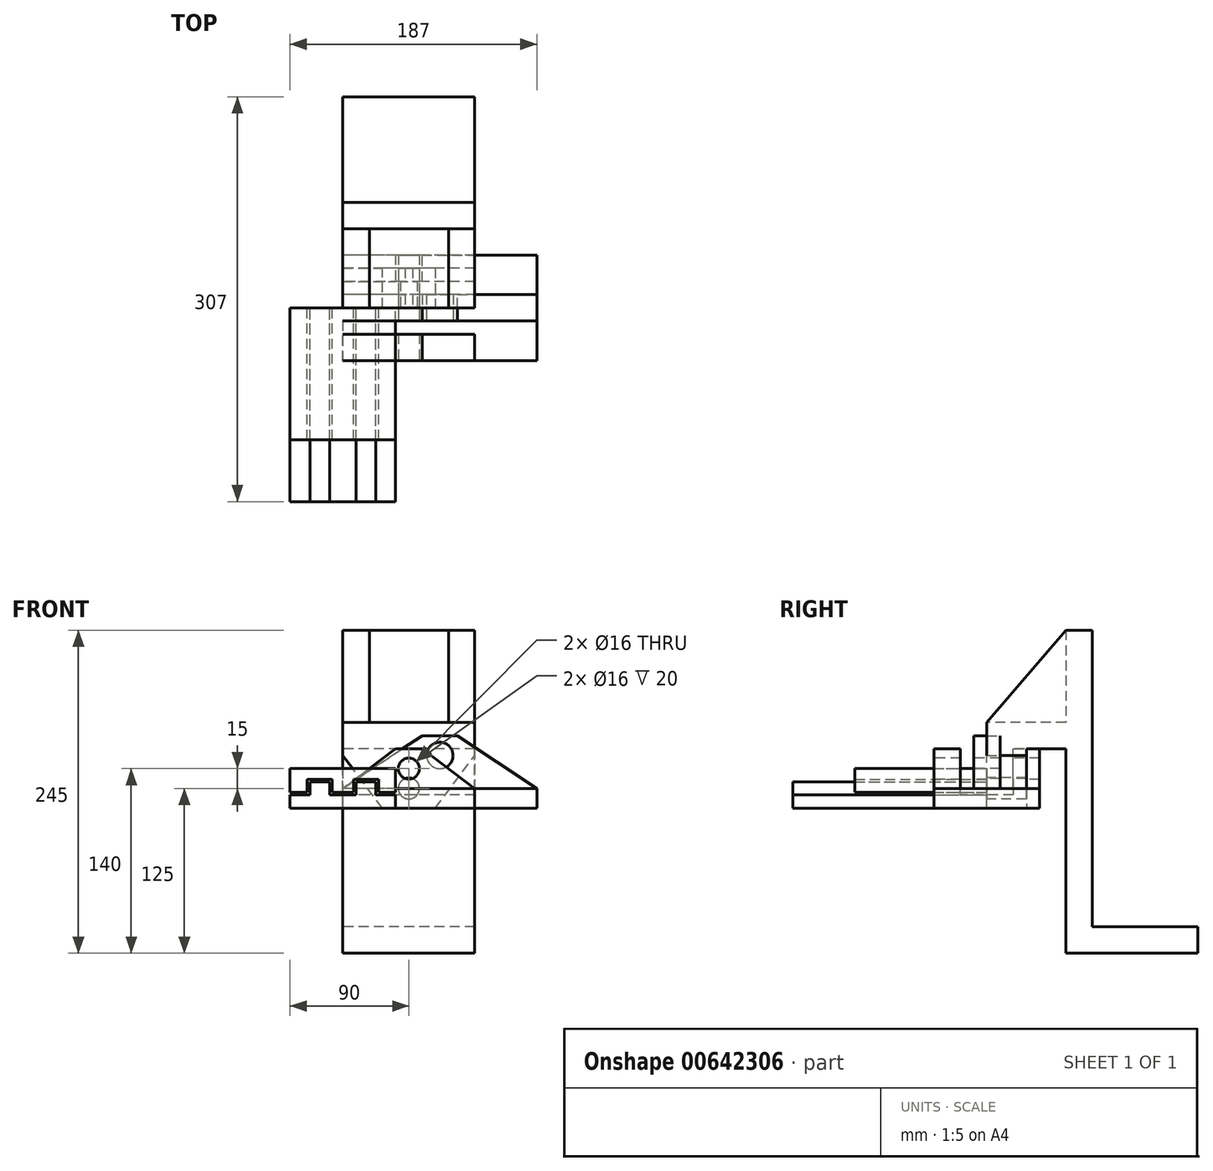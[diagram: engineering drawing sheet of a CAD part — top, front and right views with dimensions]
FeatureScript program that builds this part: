
annotation { "Feature Type Name" : "Feature", "Feature Type Description" : "" }
export const myFeature = defineFeature(function(context is Context, id is Id, definition is map)
    precondition{}
    {
        {
            var Q0;
            Q0=qCreatedBy(makeId("Right.planeOp"),FACE);
            var sketch = newSketch(context, id + "F0", { "sketchPlane" : qUnion([Q0])});
            skLineSegment(sketch, "E0", {"start": v(0, 0) * mm, "end": v(40, 0) * mm});
            skLineSegment(sketch, "E1", {"start": v(40, 0) * mm, "end": v(40, 15) * mm});
            skLineSegment(sketch, "E2", {"start": v(40, 15) * mm, "end": v(10, 15) * mm});
            skLineSegment(sketch, "E3", {"start": v(10, 15) * mm, "end": v(10, 55) * mm});
            skLineSegment(sketch, "E4", {"start": v(10, 55) * mm, "end": v(-10, 55) * mm});
            skLineSegment(sketch, "E5", {"start": v(-10, 55) * mm, "end": v(-10, 15) * mm});
            skLineSegment(sketch, "E6", {"start": v(-10, 15) * mm, "end": v(-40, 15) * mm});
            skLineSegment(sketch, "E7", {"start": v(-40, 15) * mm, "end": v(-40, 0) * mm});
            skLineSegment(sketch, "E8", {"start": v(-40, 0) * mm, "end": v(0, 0) * mm});
            skSolve(sketch);
        }
        {
            var Q0;
            Q0=makeQuery(id+"F0.imprint","IMPRINT",FACE,{"disambiguationData":[TD([[makeQuery(id+"F0.imprint","IMPRINT",EDGE,{"derivedFrom":sQuery(id+"F0.wireOp",EDGE,"E0")}),1.0]])]});
            extrude(context, id + "F1", {"entities" : qUnion([Q0]), "depth" : 147 * mm, "offsetDistance" : 25 * mm});
        }
        {
            var Q0;
            Q0=makeQuery(id+"F1.opExtrude","CAP_EDGE",EDGE,{"disambiguationData":[OSD([sQuery(id+"F0.wireOp",EDGE,"E4")])],"isStart":false});
            var Q1;
            Q1=makeQuery(id+"F1.opExtrude","CAP_EDGE",EDGE,{"disambiguationData":[OSD([sQuery(id+"F0.wireOp",EDGE,"E4")])],"isStart":true});
            chamfer(context, id + "F2", {"entities" : qUnion([Q0, Q1]), "chamferType" : ChamferType.TWO_OFFSETS, "width1" : 40 * mm, "oppositeDirection" : false, "width2" : 60 * mm, "tangentPropagation" : true});
        }
        {
            var Q0;
            Q0=makeQuery(id+"F1.opExtrude","SWEPT_FACE",FACE,{"disambiguationData":[OSD([sQuery(id+"F0.wireOp",EDGE,"E5")])]});
            var sketch = newSketch(context, id + "F3", { "sketchPlane" : qUnion([Q0])});
            skCircle(sketch, "E9", {"center": v(73.5, 40) * mm, "radius": 10 * mm});
            skPoint(sketch, "E9.centerSnap0", {"position": v(73.5, 55) * mm});
            skSolve(sketch);
        }
        {
            var Q0;
            Q0=makeQuery(id+"F3.imprint","IMPRINT",FACE,{"disambiguationData":[TD([[makeQuery(id+"F3.imprint","IMPRINT",EDGE,{"derivedFrom":sQuery(id+"F3.wireOp",EDGE,"E9")}),1.0]])]});
            extrude(context, id + "F4", {"entities" : qUnion([Q0]), "operationType" : NewBodyOperationType.REMOVE, "endBound" : BoundingType.THROUGH_ALL, "oppositeDirection" : true, "depth" : 25 * mm, "offsetDistance" : 25 * mm});
        }
        {
            var Q0;
            Q0=qCreatedBy(makeId("Front.planeOp"),FACE);
            var sketch = newSketch(context, id + "F5", { "sketchPlane" : qUnion([Q0])});
            skLineSegment(sketch, "E10", {"start": v(0, 0) * mm, "end": v(40, 0) * mm});
            skLineSegment(sketch, "E11", {"start": v(40, 0) * mm, "end": v(40, 10) * mm});
            skLineSegment(sketch, "E12", {"start": v(40, 10) * mm, "end": v(25, 10) * mm});
            skLineSegment(sketch, "E13", {"start": v(25, 10) * mm, "end": v(25, 20) * mm});
            skLineSegment(sketch, "E14", {"start": v(25, 20) * mm, "end": v(10, 20) * mm});
            skLineSegment(sketch, "E15", {"start": v(10, 20) * mm, "end": v(10, 10) * mm});
            skLineSegment(sketch, "E16", {"start": v(10, 10) * mm, "end": v(-10, 10) * mm});
            skLineSegment(sketch, "E17", {"start": v(-10, 10) * mm, "end": v(-10, 20) * mm});
            skLineSegment(sketch, "E18", {"start": v(-10, 20) * mm, "end": v(-25, 20) * mm});
            skLineSegment(sketch, "E19", {"start": v(-25, 20) * mm, "end": v(-25, 10) * mm});
            skLineSegment(sketch, "E20", {"start": v(-25, 10) * mm, "end": v(-40, 10) * mm});
            skLineSegment(sketch, "E21", {"start": v(-40, 10) * mm, "end": v(-40, 0) * mm});
            skLineSegment(sketch, "E22", {"start": v(-40, 0) * mm, "end": v(0, 0) * mm});
            skLineSegment(sketch, "E23", {"start": v(-40, 12) * mm, "end": v(-27, 12) * mm});
            skLineSegment(sketch, "E24", {"start": v(-27, 12) * mm, "end": v(-27, 22) * mm});
            skLineSegment(sketch, "E25", {"start": v(-27, 22) * mm, "end": v(-8, 22) * mm});
            skLineSegment(sketch, "E26", {"start": v(-8, 22) * mm, "end": v(-8, 12) * mm});
            skLineSegment(sketch, "E27", {"start": v(-8, 12) * mm, "end": v(8, 12) * mm});
            skLineSegment(sketch, "E28", {"start": v(8, 12) * mm, "end": v(8, 22) * mm});
            skLineSegment(sketch, "E29", {"start": v(8, 22) * mm, "end": v(27, 22) * mm});
            skLineSegment(sketch, "E30", {"start": v(27, 22) * mm, "end": v(27, 12) * mm});
            skLineSegment(sketch, "E31", {"start": v(27, 12) * mm, "end": v(40, 12) * mm});
            skLineSegment(sketch, "E32", {"start": v(40, 12) * mm, "end": v(40, 30) * mm});
            skLineSegment(sketch, "E33", {"start": v(40, 30) * mm, "end": v(-40, 30) * mm});
            skLineSegment(sketch, "E34", {"start": v(-40, 30) * mm, "end": v(-40, 12) * mm});
            skSolve(sketch);
        }
        {
            var Q0;
            Q0=makeQuery(id+"F5.imprint","IMPRINT",FACE,{"disambiguationData":[TD([[makeQuery(id+"F5.imprint","IMPRINT",EDGE,{"derivedFrom":sQuery(id+"F5.wireOp",EDGE,"E10")}),1.0]])]});
            extrude(context, id + "F6", {"entities" : qUnion([Q0]), "depth" : 147 * mm, "offsetDistance" : 25 * mm});
        }
        {
            var Q0;
            Q0=makeQuery(id+"F5.imprint","IMPRINT",FACE,{"disambiguationData":[TD([[makeQuery(id+"F5.imprint","IMPRINT",EDGE,{"derivedFrom":sQuery(id+"F5.wireOp",EDGE,"E23")}),1.0]])]});
            extrude(context, id + "F7", {"entities" : qUnion([Q0]), "depth" : 100 * mm, "offsetDistance" : 25 * mm});
        }
        {
            var Q0;
            Q0=qCreatedBy(makeId("Right.planeOp"),FACE);
            var sketch = newSketch(context, id + "F8", { "sketchPlane" : qUnion([Q0])});
            skLineSegment(sketch, "E35", {"start": v(0, 0) * mm, "end": v(40, 0) * mm});
            skLineSegment(sketch, "E36", {"start": v(40, 0) * mm, "end": v(40, 45) * mm});
            skLineSegment(sketch, "E37", {"start": v(40, 45) * mm, "end": v(20, 45) * mm});
            skLineSegment(sketch, "E38", {"start": v(20, 45) * mm, "end": v(20, 10) * mm});
            skLineSegment(sketch, "E39", {"start": v(20, 10) * mm, "end": v(-20, 10) * mm});
            skLineSegment(sketch, "E40", {"start": v(-20, 10) * mm, "end": v(-20, 45) * mm});
            skLineSegment(sketch, "E41", {"start": v(-20, 45) * mm, "end": v(-40, 45) * mm});
            skLineSegment(sketch, "E42", {"start": v(-40, 45) * mm, "end": v(-40, 0) * mm});
            skLineSegment(sketch, "E43", {"start": v(-40, 0) * mm, "end": v(0, 0) * mm});
            skSolve(sketch);
        }
        {
            var Q0;
            Q0=makeQuery(id+"F8.imprint","IMPRINT",FACE,{"disambiguationData":[TD([[makeQuery(id+"F8.imprint","IMPRINT",EDGE,{"derivedFrom":sQuery(id+"F8.wireOp",EDGE,"E35")}),1.0]])]});
            extrude(context, id + "F9", {"entities" : qUnion([Q0]), "depth" : 100 * mm, "offsetDistance" : 25 * mm});
        }
        {
            var Q0;
            Q0=makeQuery(id+"F9.opExtrude","SWEPT_FACE",FACE,{"disambiguationData":[OSD([sQuery(id+"F8.wireOp",EDGE,"E42")])]});
            var sketch = newSketch(context, id + "F10", { "sketchPlane" : qUnion([Q0])});
            skCircle(sketch, "E44", {"center": v(50, 30) * mm, "radius": 8 * mm});
            skPoint(sketch, "E44.centerSnap0", {"position": v(100, 22.5) * mm});
            skPoint(sketch, "E44.centerSnap1", {"position": v(50, 45) * mm});
            skSolve(sketch);
        }
        {
            var Q0;
            Q0=makeQuery(id+"F10.imprint","IMPRINT",FACE,{"disambiguationData":[TD([[makeQuery(id+"F10.imprint","IMPRINT",EDGE,{"derivedFrom":sQuery(id+"F10.wireOp",EDGE,"E44")}),1.0]])]});
            extrude(context, id + "F11", {"entities" : qUnion([Q0]), "operationType" : NewBodyOperationType.REMOVE, "endBound" : BoundingType.THROUGH_ALL, "oppositeDirection" : true, "depth" : 25 * mm, "offsetDistance" : 25 * mm});
        }
        {
            var Q0;
            Q0=makeQuery(id+"F9.opExtrude","CAP_EDGE",EDGE,{"disambiguationData":[OSD([sQuery(id+"F8.wireOp",EDGE,"E41")])],"isStart":false});
            var Q1;
            Q1=makeQuery(id+"F9.opExtrude","CAP_EDGE",EDGE,{"disambiguationData":[OSD([sQuery(id+"F8.wireOp",EDGE,"E37")])],"isStart":false});
            chamfer(context, id + "F12", {"entities" : qUnion([Q0, Q1]), "chamferType" : ChamferType.TWO_OFFSETS, "width1" : 30 * mm, "oppositeDirection" : false, "width2" : 40 * mm, "tangentPropagation" : true});
        }
        {
            var Q0;
            Q0=makeQuery(id+"F9.opExtrude","CAP_EDGE",EDGE,{"disambiguationData":[OSD([sQuery(id+"F8.wireOp",EDGE,"E37")])],"isStart":true});
            var Q1;
            Q1=makeQuery(id+"F9.opExtrude","CAP_EDGE",EDGE,{"disambiguationData":[OSD([sQuery(id+"F8.wireOp",EDGE,"E41")])],"isStart":true});
            chamfer(context, id + "F13", {"entities" : qUnion([Q0, Q1]), "chamferType" : ChamferType.TWO_OFFSETS, "width1" : 40 * mm, "oppositeDirection" : false, "width2" : 30 * mm, "tangentPropagation" : true});
        }
        {
            var Q0;
            Q0=qCreatedBy(makeId("Right.planeOp"),FACE);
            var sketch = newSketch(context, id + "F14", { "sketchPlane" : qUnion([Q0])});
            skLineSegment(sketch, "E45", {"start": v(0, 0) * mm, "end": v(30, 0) * mm});
            skLineSegment(sketch, "E46", {"start": v(30, 0) * mm, "end": v(30, 45) * mm});
            skLineSegment(sketch, "E47", {"start": v(30, 45) * mm, "end": v(60, 45) * mm});
            skLineSegment(sketch, "E48", {"start": v(60, 45) * mm, "end": v(60, -110) * mm});
            skLineSegment(sketch, "E49", {"start": v(60, -110) * mm, "end": v(160, -110) * mm});
            skLineSegment(sketch, "E50", {"start": v(160, -110) * mm, "end": v(160, -90) * mm});
            skLineSegment(sketch, "E51", {"start": v(160, -90) * mm, "end": v(80, -90) * mm});
            skLineSegment(sketch, "E52", {"start": v(80, -90) * mm, "end": v(80, 135) * mm});
            skLineSegment(sketch, "E53", {"start": v(80, 135) * mm, "end": v(60, 135) * mm});
            skLineSegment(sketch, "E54", {"start": v(60, 135) * mm, "end": v(60, 65) * mm});
            skLineSegment(sketch, "E55", {"start": v(60, 65) * mm, "end": v(0, 65) * mm});
            skLineSegment(sketch, "E56", {"start": v(0, 65) * mm, "end": v(0, 0) * mm});
            skSolve(sketch);
        }
        {
            var Q0;
            Q0=makeQuery(id+"F14.imprint","IMPRINT",FACE,{"disambiguationData":[TD([[makeQuery(id+"F14.imprint","IMPRINT",EDGE,{"derivedFrom":sQuery(id+"F14.wireOp",EDGE,"E45")}),1.0]])]});
            extrude(context, id + "F15", {"entities" : qUnion([Q0]), "depth" : 100 * mm, "offsetDistance" : 25 * mm});
        }
        {
            var Q0;
            Q0=makeQuery(id+"F15.opExtrude","SWEPT_FACE",FACE,{"disambiguationData":[OSD([sQuery(id+"F14.wireOp",EDGE,"E56")])]});
            var sketch = newSketch(context, id + "F16", { "sketchPlane" : qUnion([Q0])});
            skCircle(sketch, "E57", {"center": v(50, 15) * mm, "radius": 8 * mm});
            skPoint(sketch, "E57.centerSnap0", {"position": v(50, 0) * mm});
            skSolve(sketch);
        }
        {
            var Q0;
            Q0=makeQuery(id+"F16.imprint","IMPRINT",FACE,{"disambiguationData":[TD([[makeQuery(id+"F16.imprint","IMPRINT",EDGE,{"derivedFrom":sQuery(id+"F16.wireOp",EDGE,"E57")}),1.0]])]});
            var Q1;
            Q1=makeQuery(id+"F15.opExtrude","SWEPT_FACE",FACE,{"disambiguationData":[OSD([sQuery(id+"F14.wireOp",EDGE,"E46")])]});
            extrude(context, id + "F17", {"entities" : qUnion([Q0]), "operationType" : NewBodyOperationType.REMOVE, "endBound" : BoundingType.UP_TO_SURFACE, "oppositeDirection" : true, "depth" : 25 * mm, "endBoundEntityFace" : qUnion([Q1]), "offsetDistance" : 25 * mm});
        }
        {
            var Q0;
            Q0=makeQuery(id+"F15.opExtrude","CAP_EDGE",EDGE,{"disambiguationData":[OSD([sQuery(id+"F14.wireOp",EDGE,"E45")])],"isStart":false});
            chamfer(context, id + "F18", {"entities" : qUnion([Q0]), "chamferType" : ChamferType.TWO_OFFSETS, "width1" : 40 * mm, "oppositeDirection" : false, "width2" : 30 * mm, "tangentPropagation" : true});
        }
        {
            var Q0;
            Q0=makeQuery(id+"F15.opExtrude","CAP_EDGE",EDGE,{"disambiguationData":[OSD([sQuery(id+"F14.wireOp",EDGE,"E45")])],"isStart":true});
            chamfer(context, id + "F19", {"entities" : qUnion([Q0]), "chamferType" : ChamferType.TWO_OFFSETS, "width1" : 30 * mm, "oppositeDirection" : false, "width2" : 40 * mm, "tangentPropagation" : true});
        }
        {
            var Q0;
            Q0=makeQuery(id+"F15.opExtrude","CAP_FACE",FACE,{"disambiguationData":[OSD([sQuery(id+"F14.wireOp",EDGE,"E45"),sQuery(id+"F14.wireOp",EDGE,"E46"),sQuery(id+"F14.wireOp",EDGE,"E47"),sQuery(id+"F14.wireOp",EDGE,"E48"),sQuery(id+"F14.wireOp",EDGE,"E49"),sQuery(id+"F14.wireOp",EDGE,"E50"),sQuery(id+"F14.wireOp",EDGE,"E51"),sQuery(id+"F14.wireOp",EDGE,"E52"),sQuery(id+"F14.wireOp",EDGE,"E53"),sQuery(id+"F14.wireOp",EDGE,"E54"),sQuery(id+"F14.wireOp",EDGE,"E55"),sQuery(id+"F14.wireOp",EDGE,"E56")])],"isStart":false});
            var sketch = newSketch(context, id + "F20", { "sketchPlane" : qUnion([Q0])});
            skLineSegment(sketch, "E58", {"start": v(0, 65) * mm, "end": v(60, 135) * mm});
            skSolve(sketch);
        }
        {
            var Q0;
            Q0=makeQuery(id+"F20.imprint","IMPRINT",FACE,{"disambiguationData":[TD([[makeQuery(id+"F20.imprint","IMPRINT",EDGE,{"derivedFrom":sQuery(id+"F20.wireOp",EDGE,"E58")}),-1.0]])]});
            extrude(context, id + "F21", {"entities" : qUnion([Q0]), "operationType" : NewBodyOperationType.ADD, "oppositeDirection" : true, "depth" : 20 * mm, "offsetDistance" : 25 * mm});
        }
        {
            var Q0;
            Q0=makeQuery(id+"F15.opExtrude","CAP_FACE",FACE,{"disambiguationData":[OSD([sQuery(id+"F14.wireOp",EDGE,"E45"),sQuery(id+"F14.wireOp",EDGE,"E46"),sQuery(id+"F14.wireOp",EDGE,"E47"),sQuery(id+"F14.wireOp",EDGE,"E48"),sQuery(id+"F14.wireOp",EDGE,"E49"),sQuery(id+"F14.wireOp",EDGE,"E50"),sQuery(id+"F14.wireOp",EDGE,"E51"),sQuery(id+"F14.wireOp",EDGE,"E52"),sQuery(id+"F14.wireOp",EDGE,"E53"),sQuery(id+"F14.wireOp",EDGE,"E54"),sQuery(id+"F14.wireOp",EDGE,"E55"),sQuery(id+"F14.wireOp",EDGE,"E56")])],"isStart":true});
            var sketch = newSketch(context, id + "F22", { "sketchPlane" : qUnion([Q0])});
            skLineSegment(sketch, "E59", {"start": v(-60, 135) * mm, "end": v(0, 65) * mm});
            skSolve(sketch);
        }
        {
            var Q0;
            Q0=makeQuery(id+"F22.imprint","IMPRINT",FACE,{"disambiguationData":[TD([[makeQuery(id+"F22.imprint","IMPRINT",EDGE,{"derivedFrom":sQuery(id+"F22.wireOp",EDGE,"E59")}),-1.0]])]});
            extrude(context, id + "F23", {"entities" : qUnion([Q0]), "operationType" : NewBodyOperationType.ADD, "oppositeDirection" : true, "depth" : 20 * mm, "offsetDistance" : 25 * mm});
        }
    });
